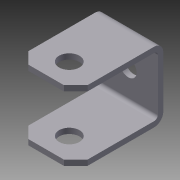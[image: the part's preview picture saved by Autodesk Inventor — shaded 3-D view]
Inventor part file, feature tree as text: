
AUTODESK INVENTOR PART (.ipt)
format: ipt  version: 2012 (Build 160160000, 160)  size: 130,048 bytes
history: native  units: in
note: dims shown in document units (in); Inventor stores cm internally (conversion verified against a paired STEP export)
features: other x2, hole x1, thicken_offset x1, imported_body x1, sketch x1
ambient origin geometry x8: Origin, YZ Plane, XZ Plane, XY Plane, X Axis, Y Axis, Z Axis, Center Point
feature tree (6):
  other  "U-Bracket"
  other  "U-Bracket1"
  hole  "Hole1"  [1 undecoded]
  thicken_offset  "Thicken1"
  imported_body  "Base1"
  sketch  "Sketch1"  dims[d0=0.14in d1=0.14in d2=0.75in d3=0.375in d4=0.25in d5=0.5635in d6=1.0in d7=0.8108in d9=0.017in d12=0.016in]
note: 1 required parameter value undecoded (feature->parameter linkage not recoverable at this tier; creation-order binding heuristic only, values carry confidence <= 0.55)
